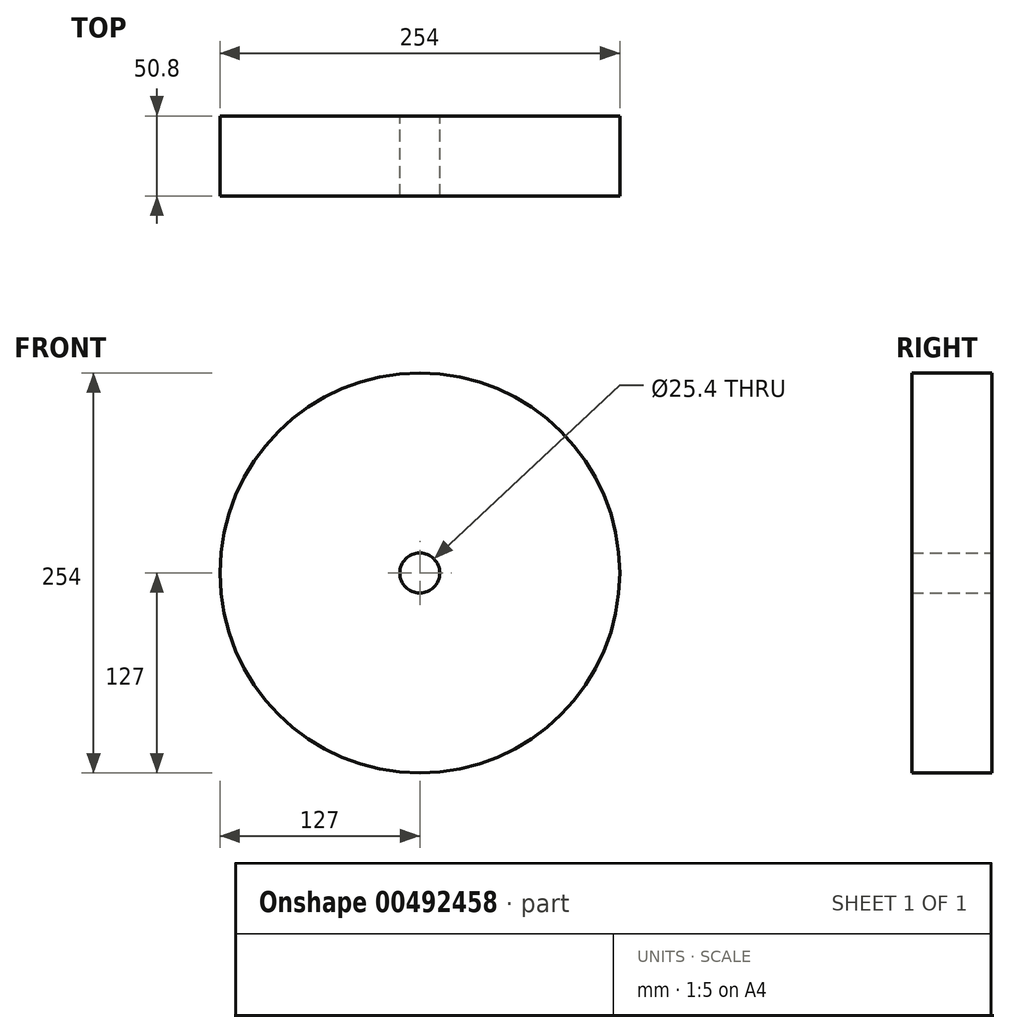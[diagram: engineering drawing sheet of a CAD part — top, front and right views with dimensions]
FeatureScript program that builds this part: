
annotation { "Feature Type Name" : "Feature", "Feature Type Description" : "" }
export const myFeature = defineFeature(function(context is Context, id is Id, definition is map)
    precondition{}
    {
        {
            var Q0;
            Q0=qCreatedBy(makeId("Front.planeOp"),FACE);
            var sketch = newSketch(context, id + "F0", { "sketchPlane" : qUnion([Q0])});
            skCircle(sketch, "E0", {"center": v(0, 0) * mm, "radius": 127 * mm});
            skCircle(sketch, "E1", {"center": v(0, 0) * mm, "radius": 12.7 * mm});
            skSolve(sketch);
        }
        {
            var Q0;
            Q0=qSketchRegion(id+"F0",true);
            extrude(context, id + "F1", {"entities" : qUnion([Q0]), "endBound" : BoundingType.SYMMETRIC, "depth" : 50.8 * mm});
        }
    });
